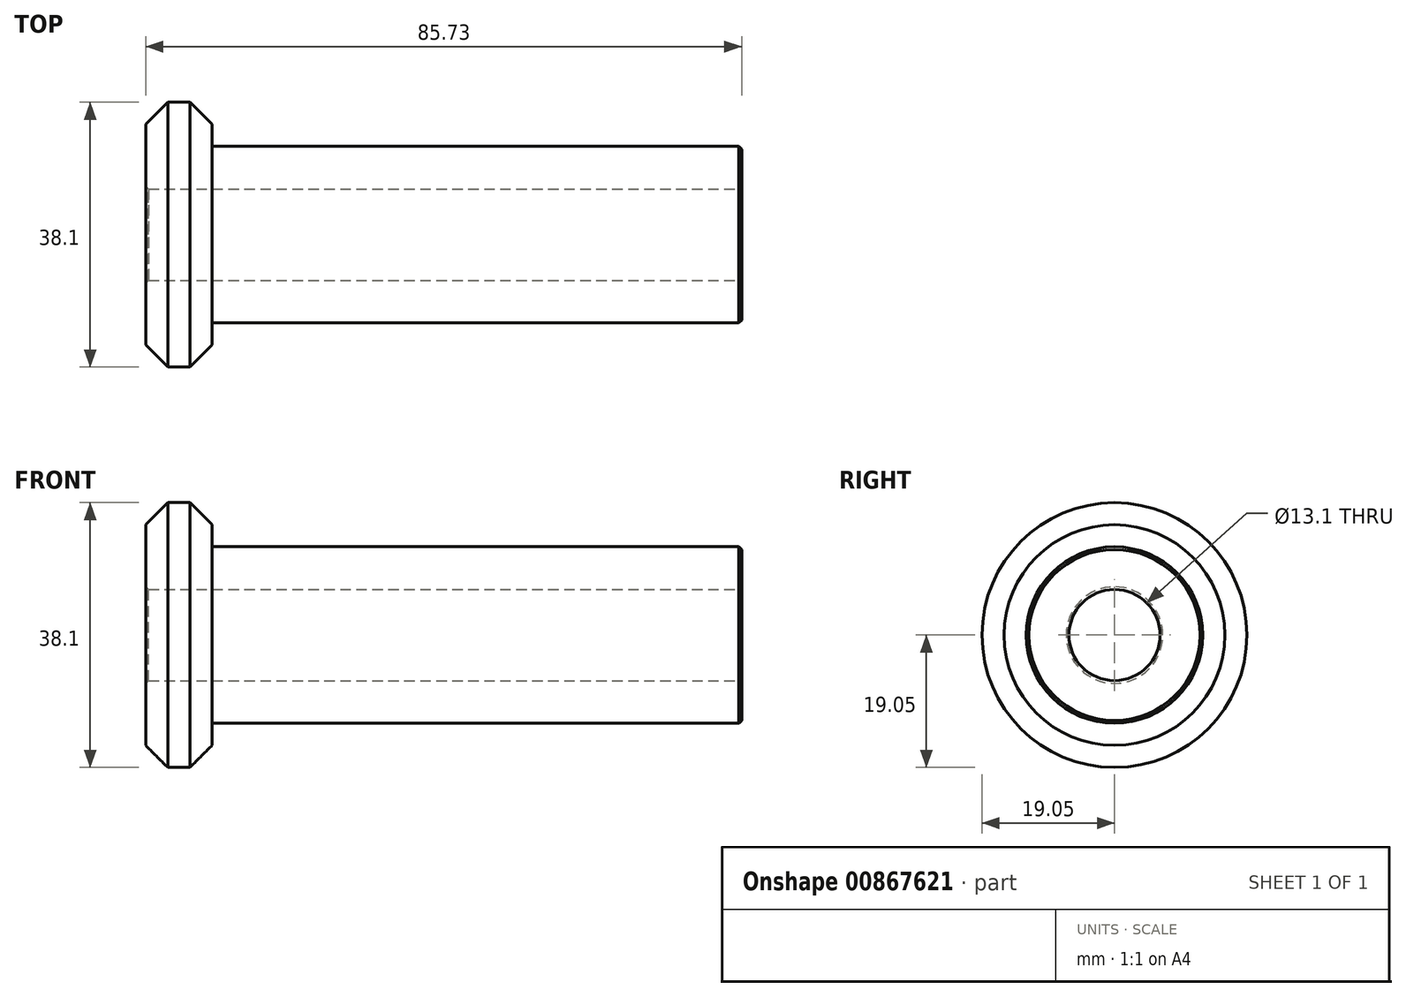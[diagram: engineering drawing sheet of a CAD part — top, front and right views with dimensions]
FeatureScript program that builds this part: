
annotation { "Feature Type Name" : "Feature", "Feature Type Description" : "" }
export const myFeature = defineFeature(function(context is Context, id is Id, definition is map)
    precondition{}
    {
        {
            var Q0;
            Q0=qCreatedBy(makeId("Right.planeOp"),FACE);
            var sketch = newSketch(context, id + "F0", { "sketchPlane" : qUnion([Q0])});
            skCircle(sketch, "E0", {"center": v(0, 0) * mm, "radius": 19.05 * mm});
            skSolve(sketch);
        }
        {
            var Q0;
            Q0 = qSketchRegion(id + "F0", true);
            extrude(context, id + "F1", {"entities" : qUnion([Q0]), "depth" : 9.52 * mm, "offsetDistance" : 25.4 * mm});
        }
        {
            var Q0;
            Q0=makeQuery(id+"F1.opExtrude","CAP_EDGE",EDGE,{"disambiguationData":[OSD([sQuery(id+"F0.wireOp",EDGE,"E0")])],"isStart":false});
            var Q1;
            Q1=makeQuery(id+"F1.opExtrude","CAP_EDGE",EDGE,{"disambiguationData":[OSD([sQuery(id+"F0.wireOp",EDGE,"E0")])],"isStart":true});
            chamfer(context, id + "F2", {"entities" : qUnion([Q0, Q1]), "width" : 3.17 * mm, "tangentPropagation" : true});
        }
        {
            var Q0;
            Q0=makeQuery(id+"F1.opExtrude","CAP_FACE",FACE,{"disambiguationData":[OSD([sQuery(id+"F0.wireOp",EDGE,"E0")])],"isStart":false});
            var sketch = newSketch(context, id + "F3", { "sketchPlane" : qUnion([Q0])});
            skCircle(sketch, "E1", {"center": v(0, 0) * mm, "radius": 12.7 * mm});
            skSolve(sketch);
        }
        {
            var Q0;
            Q0 = qSketchRegion(id + "F3", true);
            extrude(context, id + "F4", {"entities" : qUnion([Q0]), "operationType" : NewBodyOperationType.ADD, "depth" : 76.2 * mm, "offsetDistance" : 25.4 * mm});
        }
        {
            var Q0;
            Q0=makeQuery(id+"F4.opExtrude","CAP_FACE",FACE,{"disambiguationData":[OSD([sQuery(id+"F3.wireOp",EDGE,"E1")])],"isStart":false});
            var sketch = newSketch(context, id + "F5", { "sketchPlane" : qUnion([Q0])});
            skCircle(sketch, "E2", {"center": v(0, 0) * mm, "radius": 6.55 * mm});
            skSolve(sketch);
        }
        {
            var Q0;
            Q0 = qSketchRegion(id + "F5", true);
            extrude(context, id + "F6", {"entities" : qUnion([Q0]), "operationType" : NewBodyOperationType.REMOVE, "endBound" : BoundingType.THROUGH_ALL, "oppositeDirection" : true, "depth" : 25.4 * mm, "offsetDistance" : 25.4 * mm});
        }
        {
            var Q0;
            Q0=makeQuery(id+"F4.opExtrude","CAP_EDGE",EDGE,{"disambiguationData":[OSD([sQuery(id+"F3.wireOp",EDGE,"E1")])],"isStart":false});
            var Q1;
            Q1=makeQuery(id+"F6.boolean.opBoolean","COPY",EDGE,{"derivedFrom":makeQuery(id+"F6.opExtrude","CAP_EDGE",EDGE,{"disambiguationData":[OSD([sQuery(id+"F5.wireOp",EDGE,"E2")])],"isStart":true})});
            var Q2;
            Q2=makeQuery(id+"F6.boolean.opBoolean","INTERSECT",EDGE,{"derivedFrom":[makeQuery(id+"F1.opExtrude","CAP_FACE",FACE,{"disambiguationData":[OSD([sQuery(id+"F0.wireOp",EDGE,"E0")])],"isStart":true}),makeQuery(id+"F6.opExtrude","SWEPT_FACE",FACE,{"disambiguationData":[OSD([sQuery(id+"F5.wireOp",EDGE,"E2")])]})]});
            chamfer(context, id + "F7", {"entities" : qUnion([Q0, Q1, Q2]), "width" : 0.4 * mm, "tangentPropagation" : true});
        }
    });
